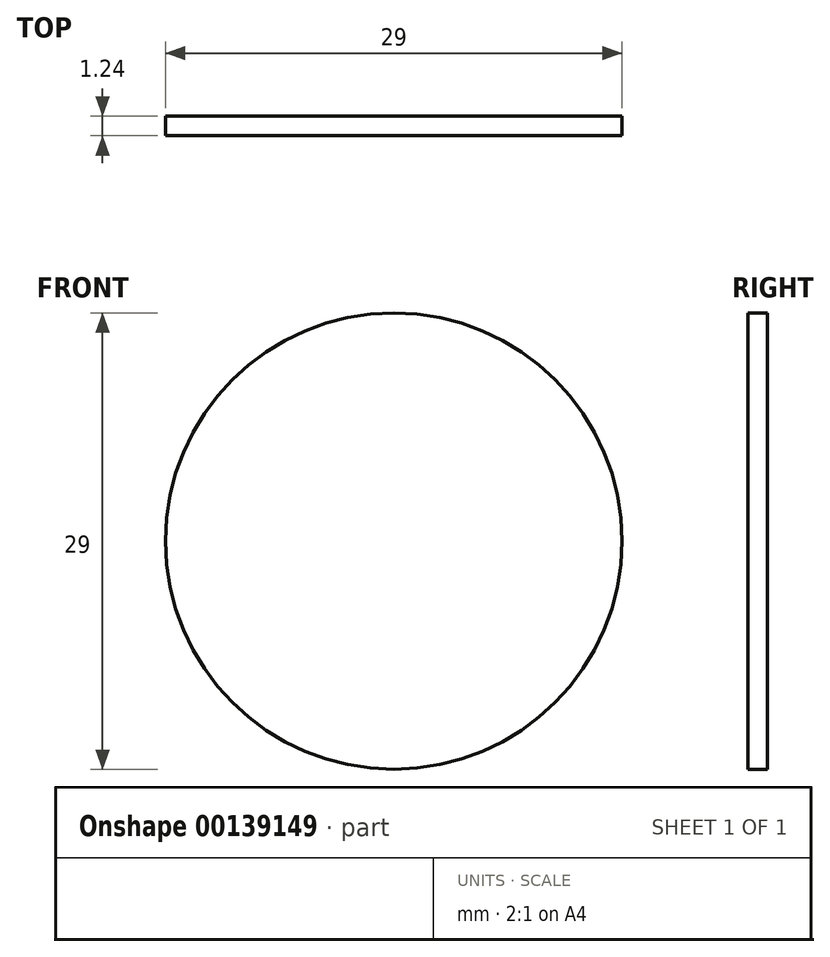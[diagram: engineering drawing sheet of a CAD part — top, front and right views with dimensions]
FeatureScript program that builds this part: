
annotation { "Feature Type Name" : "Feature", "Feature Type Description" : "" }
export const myFeature = defineFeature(function(context is Context, id is Id, definition is map)
    precondition{}
    {
        {
            var Q0;
            Q0=qCreatedBy(makeId("Front.planeOp"),FACE);
            var sketch = newSketch(context, id + "F0", { "sketchPlane" : qUnion([Q0])});
            skCircle(sketch, "E0", {"center": v(0, 0) * mm, "radius": 14.5 * mm});
            skSolve(sketch);
        }
        {
            var Q0;
            Q0 = qSketchRegion(id + "F0", true);
            extrude(context, id + "F1", {"entities" : qUnion([Q0]), "depth" : 1.24 * mm});
        }
    });
